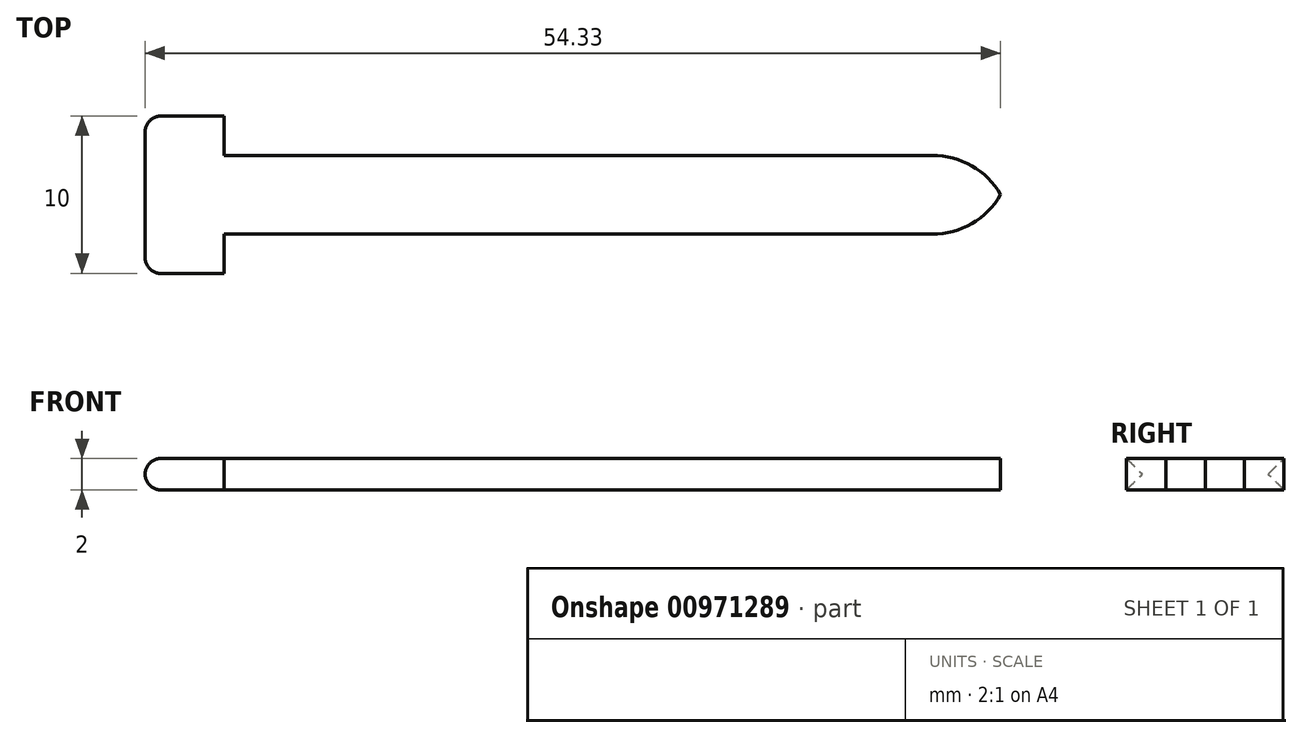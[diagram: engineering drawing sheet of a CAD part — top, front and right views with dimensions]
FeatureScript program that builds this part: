
annotation { "Feature Type Name" : "Feature", "Feature Type Description" : "" }
export const myFeature = defineFeature(function(context is Context, id is Id, definition is map)
    precondition{}
    {
        {
            var Q0;
            Q0=qCreatedBy(makeId("Top.planeOp"),FACE);
            var sketch = newSketch(context, id + "F0", { "sketchPlane" : qUnion([Q0])});
            skLineSegment(sketch, "E0.bottom", {"start": v(25, 2.5) * mm, "end": v(-25, 2.5) * mm});
            skLineSegment(sketch, "E0.top", {"start": v(25, -2.5) * mm, "end": v(-25, -2.5) * mm});
            skLineSegment(sketch, "E0.left", {"start": v(25, 2.5) * mm, "end": v(25, -2.5) * mm});
            skLineSegment(sketch, "E0.right", {"start": v(-25, 2.5) * mm, "end": v(-25, -2.5) * mm});
            skPoint(sketch, "E0.middle", {"position": v(0, 0) * mm});
            skLineSegment(sketch, "E1", {"start": v(-25, 0) * mm, "end": v(-25, -5) * mm});
            skLineSegment(sketch, "E2.bottom", {"start": v(-25, -5) * mm, "end": v(-30, -5) * mm});
            skLineSegment(sketch, "E2.top", {"start": v(-25, 5) * mm, "end": v(-30, 5) * mm});
            skLineSegment(sketch, "E2.left", {"start": v(-25, -5) * mm, "end": v(-25, 5) * mm});
            skLineSegment(sketch, "E2.right", {"start": v(-30, -5) * mm, "end": v(-30, 5) * mm});
            skSolve(sketch);
        }
        {
            var Q0;
            {var subQ3=sQuery(id+"F0.wireOp",EDGE,"E2.bottom");Q0=makeQuery(id+"F0.imprint","IMPRINT",FACE,{"disambiguationData":[TD([[makeQuery(id+"F0.imprint","IMPRINT",EDGE,{"derivedFrom":subQ3}),-1.0]])]});}
            var Q1;
            {var subQ3=sQuery(id+"F0.wireOp",EDGE,"E0.bottom");Q1=makeQuery(id+"F0.imprint","IMPRINT",FACE,{"disambiguationData":[TD([[makeQuery(id+"F0.imprint","IMPRINT",EDGE,{"derivedFrom":subQ3}),1.0]])]});}
            extrude(context, id + "F1", {"entities" : qUnion([Q0, Q1]), "depth" : 2 * mm, "offsetDistance" : 25 * mm});
        }
        {
            var Q0;
            Q0=makeQuery(id+"F1.opExtrude","SWEPT_EDGE",EDGE,{"disambiguationData":[OSD([sQuery(id+"F0.wireOp",EDGE,"E2.bottom"),sQuery(id+"F0.wireOp",EDGE,"E2.right")])]});
            var Q1;
            Q1=makeQuery(id+"F1.opExtrude","CAP_EDGE",EDGE,{"disambiguationData":[OSD([sQuery(id+"F0.wireOp",EDGE,"E2.right")])],"isStart":false});
            var Q2;
            Q2=makeQuery(id+"F1.opExtrude","SWEPT_EDGE",EDGE,{"disambiguationData":[OSD([sQuery(id+"F0.wireOp",EDGE,"E2.top"),sQuery(id+"F0.wireOp",EDGE,"E2.right")])]});
            var Q3;
            Q3=makeQuery(id+"F1.opExtrude","CAP_EDGE",EDGE,{"disambiguationData":[OSD([sQuery(id+"F0.wireOp",EDGE,"E2.right")])],"isStart":true});
            fillet(context, id + "F2", {"entities" : qUnion([Q0, Q1, Q2, Q3]), "radius" : 1 * mm, "tangentPropagation" : true, "allowEdgeOverflow" : false});
        }
        {
            var Q0;
            Q0=makeQuery(id+"F1.opExtrude","SWEPT_EDGE",EDGE,{"disambiguationData":[OSD([sQuery(id+"F0.wireOp",EDGE,"E0.top"),sQuery(id+"F0.wireOp",EDGE,"E0.left")])]});
            var Q1;
            Q1=makeQuery(id+"F1.opExtrude","SWEPT_EDGE",EDGE,{"disambiguationData":[OSD([sQuery(id+"F0.wireOp",EDGE,"E0.bottom"),sQuery(id+"F0.wireOp",EDGE,"E0.left")])]});
            fillet(context, id + "F3", {"entities" : qUnion([Q0, Q1]), "radius" : 5 * mm, "tangentPropagation" : true, "allowEdgeOverflow" : false});
        }
    });
